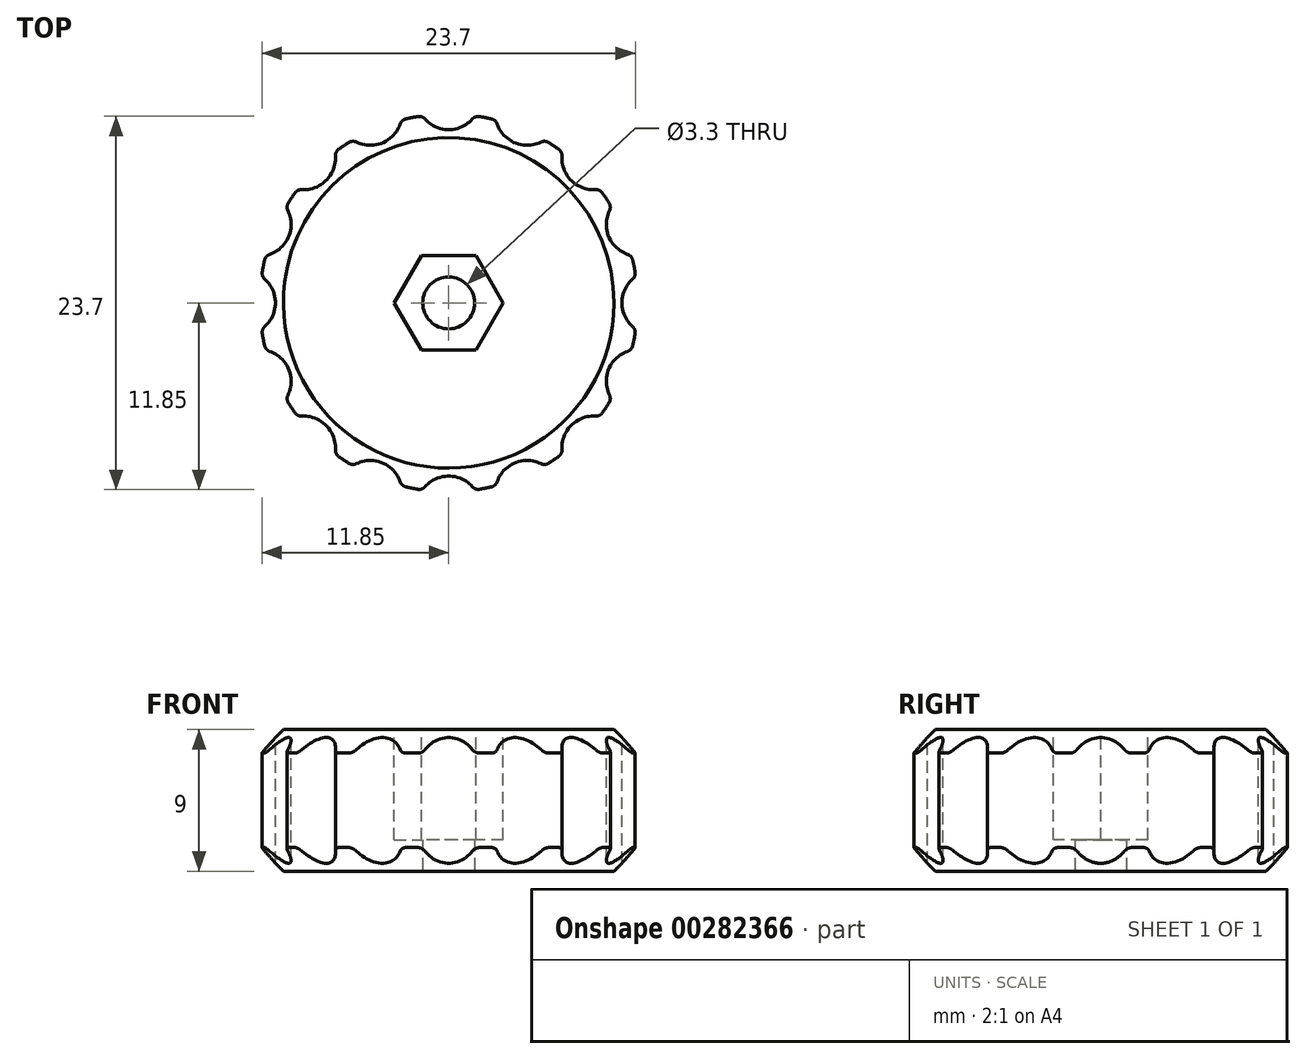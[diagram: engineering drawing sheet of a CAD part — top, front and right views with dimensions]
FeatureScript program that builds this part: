
annotation { "Feature Type Name" : "Feature", "Feature Type Description" : "" }
export const myFeature = defineFeature(function(context is Context, id is Id, definition is map)
    precondition{}
    {
        {
            var Q0;
            Q0=qCreatedBy(makeId("Top.planeOp"),FACE);
            var sketch = newSketch(context, id + "F0", { "sketchPlane" : qUnion([Q0])});
            skCircle(sketch, "E0", {"center": v(0, 0) * mm, "radius": 12 * mm});
            skCircle(sketch, "E1", {"center": v(0, 0) * mm, "radius": 1.65 * mm});
            skSolve(sketch);
        }
        {
            var Q0;
            Q0 = qSketchRegion(id + "F0", true);
            extrude(context, id + "F1", {"entities" : qUnion([Q0]), "depth" : 9 * mm});
        }
        {
            var Q0;
            Q0=makeQuery(id+"F1.opExtrude","CAP_EDGE",EDGE,{"disambiguationData":[OSD([sQuery(id+"F0.wireOp",EDGE,"E0")])],"isStart":false});
            var Q1;
            Q1=makeQuery(id+"F1.opExtrude","CAP_EDGE",EDGE,{"disambiguationData":[OSD([sQuery(id+"F0.wireOp",EDGE,"E0")])],"isStart":true});
            chamfer(context, id + "F2", {"entities" : qUnion([Q0, Q1]), "width" : 1.5 * mm, "tangentPropagation" : true});
        }
        {
            var Q0;
            Q0=makeQuery(id+"F1.opExtrude","CAP_FACE",FACE,{"disambiguationData":[OSD([sQuery(id+"F0.wireOp",EDGE,"E0"),sQuery(id+"F0.wireOp",EDGE,"E1")])],"isStart":false});
            var sketch = newSketch(context, id + "F3", { "sketchPlane" : qUnion([Q0])});
            skCircle(sketch, "E2.cCircle", {"center": v(0, 0) * mm, "radius": 3 * mm, "construction": true});
            skLineSegment(sketch, "E2.0", {"start": v(1.73, -3) * mm, "end": v(-1.73, -3) * mm});
            skLineSegment(sketch, "E2.1", {"start": v(-1.73, -3) * mm, "end": v(-3.46, 0) * mm});
            skLineSegment(sketch, "E2.2", {"start": v(-3.46, 0) * mm, "end": v(-1.73, 3) * mm});
            skLineSegment(sketch, "E2.3", {"start": v(-1.73, 3) * mm, "end": v(1.73, 3) * mm});
            skLineSegment(sketch, "E2.4", {"start": v(1.73, 3) * mm, "end": v(3.46, 0) * mm});
            skLineSegment(sketch, "E2.5", {"start": v(3.46, 0) * mm, "end": v(1.73, -3) * mm});
            skPoint(sketch, "E2.0.midPoint", {"position": v(0, -3) * mm});
            skSolve(sketch);
        }
        {
            var Q0;
            Q0 = qSketchRegion(id + "F3", true);
            extrude(context, id + "F4", {"entities" : qUnion([Q0]), "operationType" : NewBodyOperationType.REMOVE, "oppositeDirection" : true, "depth" : 7 * mm});
        }
        {
            var Q0;
            Q0=makeQuery(id+"F1.opExtrude","CAP_FACE",FACE,{"disambiguationData":[OSD([sQuery(id+"F0.wireOp",EDGE,"E0"),sQuery(id+"F0.wireOp",EDGE,"E1")])],"isStart":false});
            var sketch = newSketch(context, id + "F5", { "sketchPlane" : qUnion([Q0])});
            skLineSegment(sketch, "E3", {"start": v(0, 0) * mm, "end": v(13, 0) * mm, "construction": true});
            skCircle(sketch, "E4", {"center": v(13, 0) * mm, "radius": 2 * mm});
            skCircle(sketch, "E5.1.0", {"center": v(12.01, 4.97) * mm, "radius": 2 * mm});
            skCircle(sketch, "E5.2.0", {"center": v(9.2, 9.2) * mm, "radius": 2 * mm});
            skCircle(sketch, "E5.3.0", {"center": v(4.97, 12.01) * mm, "radius": 2 * mm});
            skCircle(sketch, "E5.4.0", {"center": v(0, 13) * mm, "radius": 2 * mm});
            skCircle(sketch, "E5.5.0", {"center": v(-4.97, 12.01) * mm, "radius": 2 * mm});
            skCircle(sketch, "E5.6.0", {"center": v(-9.2, 9.2) * mm, "radius": 2 * mm});
            skCircle(sketch, "E5.7.0", {"center": v(-12.01, 4.97) * mm, "radius": 2 * mm});
            skCircle(sketch, "E5.8.0", {"center": v(-13, 0) * mm, "radius": 2 * mm});
            skCircle(sketch, "E5.9.0", {"center": v(-12.01, -4.97) * mm, "radius": 2 * mm});
            skCircle(sketch, "E5.10.0", {"center": v(-9.2, -9.2) * mm, "radius": 2 * mm});
            skCircle(sketch, "E5.11.0", {"center": v(-4.97, -12.01) * mm, "radius": 2 * mm});
            skCircle(sketch, "E5.12.0", {"center": v(0, -13) * mm, "radius": 2 * mm});
            skCircle(sketch, "E5.13.0", {"center": v(4.97, -12.01) * mm, "radius": 2 * mm});
            skCircle(sketch, "E5.14.0", {"center": v(9.2, -9.2) * mm, "radius": 2 * mm});
            skCircle(sketch, "E5.15.0", {"center": v(12.01, -4.97) * mm, "radius": 2 * mm});
            skPoint(sketch, "E5.center", {"position": v(0, 0) * mm});
            skSolve(sketch);
        }
        {
            var Q0;
            Q0 = qSketchRegion(id + "F5", true);
            extrude(context, id + "F6", {"entities" : qUnion([Q0]), "operationType" : NewBodyOperationType.REMOVE, "endBound" : BoundingType.THROUGH_ALL, "oppositeDirection" : true, "depth" : 25 * mm});
        }
        {
            var Q0;
            Q0=makeQuery(id+"F6.boolean.opBoolean","INTERSECT",EDGE,{"disambiguationData":[OD(0.0)],"derivedFrom":[makeQuery(id+"F1.opExtrude","SWEPT_FACE",FACE,{"disambiguationData":[OSD([sQuery(id+"F0.wireOp",EDGE,"E0")])]}),makeQuery(id+"F6.opExtrude","SWEPT_FACE",FACE,{"disambiguationData":[OSD([sQuery(id+"F5.wireOp",EDGE,"E5.4.0")])]})]});
            var Q1;
            Q1=makeQuery(id+"F6.boolean.opBoolean","INTERSECT",EDGE,{"disambiguationData":[OD(1.0)],"derivedFrom":[makeQuery(id+"F1.opExtrude","SWEPT_FACE",FACE,{"disambiguationData":[OSD([sQuery(id+"F0.wireOp",EDGE,"E0")])]}),makeQuery(id+"F6.opExtrude","SWEPT_FACE",FACE,{"disambiguationData":[OSD([sQuery(id+"F5.wireOp",EDGE,"E5.3.0")])]})]});
            var Q2;
            Q2=makeQuery(id+"F6.boolean.opBoolean","INTERSECT",EDGE,{"disambiguationData":[OD(0.0)],"derivedFrom":[makeQuery(id+"F1.opExtrude","SWEPT_FACE",FACE,{"disambiguationData":[OSD([sQuery(id+"F0.wireOp",EDGE,"E0")])]}),makeQuery(id+"F6.opExtrude","SWEPT_FACE",FACE,{"disambiguationData":[OSD([sQuery(id+"F5.wireOp",EDGE,"E5.3.0")])]})]});
            var Q3;
            Q3=makeQuery(id+"F6.boolean.opBoolean","INTERSECT",EDGE,{"disambiguationData":[OD(1.0)],"derivedFrom":[makeQuery(id+"F1.opExtrude","SWEPT_FACE",FACE,{"disambiguationData":[OSD([sQuery(id+"F0.wireOp",EDGE,"E0")])]}),makeQuery(id+"F6.opExtrude","SWEPT_FACE",FACE,{"disambiguationData":[OSD([sQuery(id+"F5.wireOp",EDGE,"E5.2.0")])]})]});
            var Q4;
            Q4=makeQuery(id+"F6.boolean.opBoolean","INTERSECT",EDGE,{"disambiguationData":[OD(0.0)],"derivedFrom":[makeQuery(id+"F1.opExtrude","SWEPT_FACE",FACE,{"disambiguationData":[OSD([sQuery(id+"F0.wireOp",EDGE,"E0")])]}),makeQuery(id+"F6.opExtrude","SWEPT_FACE",FACE,{"disambiguationData":[OSD([sQuery(id+"F5.wireOp",EDGE,"E5.2.0")])]})]});
            var Q5;
            Q5=makeQuery(id+"F6.boolean.opBoolean","INTERSECT",EDGE,{"disambiguationData":[OD(1.0)],"derivedFrom":[makeQuery(id+"F1.opExtrude","SWEPT_FACE",FACE,{"disambiguationData":[OSD([sQuery(id+"F0.wireOp",EDGE,"E0")])]}),makeQuery(id+"F6.opExtrude","SWEPT_FACE",FACE,{"disambiguationData":[OSD([sQuery(id+"F5.wireOp",EDGE,"E5.1.0")])]})]});
            var Q6;
            Q6=makeQuery(id+"F6.boolean.opBoolean","INTERSECT",EDGE,{"disambiguationData":[OD(0.0)],"derivedFrom":[makeQuery(id+"F1.opExtrude","SWEPT_FACE",FACE,{"disambiguationData":[OSD([sQuery(id+"F0.wireOp",EDGE,"E0")])]}),makeQuery(id+"F6.opExtrude","SWEPT_FACE",FACE,{"disambiguationData":[OSD([sQuery(id+"F5.wireOp",EDGE,"E5.1.0")])]})]});
            var Q7;
            Q7=makeQuery(id+"F6.boolean.opBoolean","INTERSECT",EDGE,{"disambiguationData":[OD(0.0)],"derivedFrom":[makeQuery(id+"F1.opExtrude","SWEPT_FACE",FACE,{"disambiguationData":[OSD([sQuery(id+"F0.wireOp",EDGE,"E0")])]}),makeQuery(id+"F6.opExtrude","SWEPT_FACE",FACE,{"disambiguationData":[OSD([sQuery(id+"F5.wireOp",EDGE,"E4")])]})]});
            var Q8;
            Q8=makeQuery(id+"F6.boolean.opBoolean","INTERSECT",EDGE,{"disambiguationData":[OD(1.0)],"derivedFrom":[makeQuery(id+"F1.opExtrude","SWEPT_FACE",FACE,{"disambiguationData":[OSD([sQuery(id+"F0.wireOp",EDGE,"E0")])]}),makeQuery(id+"F6.opExtrude","SWEPT_FACE",FACE,{"disambiguationData":[OSD([sQuery(id+"F5.wireOp",EDGE,"E4")])]})]});
            var Q9;
            Q9=makeQuery(id+"F6.boolean.opBoolean","INTERSECT",EDGE,{"disambiguationData":[OD(0.0)],"derivedFrom":[makeQuery(id+"F1.opExtrude","SWEPT_FACE",FACE,{"disambiguationData":[OSD([sQuery(id+"F0.wireOp",EDGE,"E0")])]}),makeQuery(id+"F6.opExtrude","SWEPT_FACE",FACE,{"disambiguationData":[OSD([sQuery(id+"F5.wireOp",EDGE,"E5.15.0")])]})]});
            var Q10;
            Q10=makeQuery(id+"F6.boolean.opBoolean","INTERSECT",EDGE,{"disambiguationData":[OD(1.0)],"derivedFrom":[makeQuery(id+"F1.opExtrude","SWEPT_FACE",FACE,{"disambiguationData":[OSD([sQuery(id+"F0.wireOp",EDGE,"E0")])]}),makeQuery(id+"F6.opExtrude","SWEPT_FACE",FACE,{"disambiguationData":[OSD([sQuery(id+"F5.wireOp",EDGE,"E5.15.0")])]})]});
            var Q11;
            Q11=makeQuery(id+"F6.boolean.opBoolean","INTERSECT",EDGE,{"disambiguationData":[OD(1.0)],"derivedFrom":[makeQuery(id+"F1.opExtrude","SWEPT_FACE",FACE,{"disambiguationData":[OSD([sQuery(id+"F0.wireOp",EDGE,"E0")])]}),makeQuery(id+"F6.opExtrude","SWEPT_FACE",FACE,{"disambiguationData":[OSD([sQuery(id+"F5.wireOp",EDGE,"E5.14.0")])]})]});
            var Q12;
            Q12=makeQuery(id+"F6.boolean.opBoolean","INTERSECT",EDGE,{"disambiguationData":[OD(0.0)],"derivedFrom":[makeQuery(id+"F1.opExtrude","SWEPT_FACE",FACE,{"disambiguationData":[OSD([sQuery(id+"F0.wireOp",EDGE,"E0")])]}),makeQuery(id+"F6.opExtrude","SWEPT_FACE",FACE,{"disambiguationData":[OSD([sQuery(id+"F5.wireOp",EDGE,"E5.14.0")])]})]});
            var Q13;
            Q13=makeQuery(id+"F6.boolean.opBoolean","INTERSECT",EDGE,{"disambiguationData":[OD(1.0)],"derivedFrom":[makeQuery(id+"F1.opExtrude","SWEPT_FACE",FACE,{"disambiguationData":[OSD([sQuery(id+"F0.wireOp",EDGE,"E0")])]}),makeQuery(id+"F6.opExtrude","SWEPT_FACE",FACE,{"disambiguationData":[OSD([sQuery(id+"F5.wireOp",EDGE,"E5.13.0")])]})]});
            var Q14;
            Q14=makeQuery(id+"F6.boolean.opBoolean","INTERSECT",EDGE,{"disambiguationData":[OD(0.0)],"derivedFrom":[makeQuery(id+"F1.opExtrude","SWEPT_FACE",FACE,{"disambiguationData":[OSD([sQuery(id+"F0.wireOp",EDGE,"E0")])]}),makeQuery(id+"F6.opExtrude","SWEPT_FACE",FACE,{"disambiguationData":[OSD([sQuery(id+"F5.wireOp",EDGE,"E5.13.0")])]})]});
            var Q15;
            Q15=makeQuery(id+"F6.boolean.opBoolean","INTERSECT",EDGE,{"disambiguationData":[OD(1.0)],"derivedFrom":[makeQuery(id+"F1.opExtrude","SWEPT_FACE",FACE,{"disambiguationData":[OSD([sQuery(id+"F0.wireOp",EDGE,"E0")])]}),makeQuery(id+"F6.opExtrude","SWEPT_FACE",FACE,{"disambiguationData":[OSD([sQuery(id+"F5.wireOp",EDGE,"E5.12.0")])]})]});
            var Q16;
            Q16=makeQuery(id+"F6.boolean.opBoolean","INTERSECT",EDGE,{"disambiguationData":[OD(0.0)],"derivedFrom":[makeQuery(id+"F1.opExtrude","SWEPT_FACE",FACE,{"disambiguationData":[OSD([sQuery(id+"F0.wireOp",EDGE,"E0")])]}),makeQuery(id+"F6.opExtrude","SWEPT_FACE",FACE,{"disambiguationData":[OSD([sQuery(id+"F5.wireOp",EDGE,"E5.12.0")])]})]});
            var Q17;
            Q17=makeQuery(id+"F6.boolean.opBoolean","INTERSECT",EDGE,{"disambiguationData":[OD(1.0)],"derivedFrom":[makeQuery(id+"F1.opExtrude","SWEPT_FACE",FACE,{"disambiguationData":[OSD([sQuery(id+"F0.wireOp",EDGE,"E0")])]}),makeQuery(id+"F6.opExtrude","SWEPT_FACE",FACE,{"disambiguationData":[OSD([sQuery(id+"F5.wireOp",EDGE,"E5.11.0")])]})]});
            var Q18;
            Q18=makeQuery(id+"F6.boolean.opBoolean","INTERSECT",EDGE,{"disambiguationData":[OD(0.0)],"derivedFrom":[makeQuery(id+"F1.opExtrude","SWEPT_FACE",FACE,{"disambiguationData":[OSD([sQuery(id+"F0.wireOp",EDGE,"E0")])]}),makeQuery(id+"F6.opExtrude","SWEPT_FACE",FACE,{"disambiguationData":[OSD([sQuery(id+"F5.wireOp",EDGE,"E5.11.0")])]})]});
            var Q19;
            Q19=makeQuery(id+"F6.boolean.opBoolean","INTERSECT",EDGE,{"disambiguationData":[OD(1.0)],"derivedFrom":[makeQuery(id+"F1.opExtrude","SWEPT_FACE",FACE,{"disambiguationData":[OSD([sQuery(id+"F0.wireOp",EDGE,"E0")])]}),makeQuery(id+"F6.opExtrude","SWEPT_FACE",FACE,{"disambiguationData":[OSD([sQuery(id+"F5.wireOp",EDGE,"E5.10.0")])]})]});
            var Q20;
            Q20=makeQuery(id+"F6.boolean.opBoolean","INTERSECT",EDGE,{"disambiguationData":[OD(0.0)],"derivedFrom":[makeQuery(id+"F1.opExtrude","SWEPT_FACE",FACE,{"disambiguationData":[OSD([sQuery(id+"F0.wireOp",EDGE,"E0")])]}),makeQuery(id+"F6.opExtrude","SWEPT_FACE",FACE,{"disambiguationData":[OSD([sQuery(id+"F5.wireOp",EDGE,"E5.10.0")])]})]});
            var Q21;
            Q21=makeQuery(id+"F6.boolean.opBoolean","INTERSECT",EDGE,{"disambiguationData":[OD(1.0)],"derivedFrom":[makeQuery(id+"F1.opExtrude","SWEPT_FACE",FACE,{"disambiguationData":[OSD([sQuery(id+"F0.wireOp",EDGE,"E0")])]}),makeQuery(id+"F6.opExtrude","SWEPT_FACE",FACE,{"disambiguationData":[OSD([sQuery(id+"F5.wireOp",EDGE,"E5.9.0")])]})]});
            var Q22;
            Q22=makeQuery(id+"F6.boolean.opBoolean","INTERSECT",EDGE,{"disambiguationData":[OD(0.0)],"derivedFrom":[makeQuery(id+"F1.opExtrude","SWEPT_FACE",FACE,{"disambiguationData":[OSD([sQuery(id+"F0.wireOp",EDGE,"E0")])]}),makeQuery(id+"F6.opExtrude","SWEPT_FACE",FACE,{"disambiguationData":[OSD([sQuery(id+"F5.wireOp",EDGE,"E5.9.0")])]})]});
            var Q23;
            Q23=makeQuery(id+"F6.boolean.opBoolean","INTERSECT",EDGE,{"disambiguationData":[OD(1.0)],"derivedFrom":[makeQuery(id+"F1.opExtrude","SWEPT_FACE",FACE,{"disambiguationData":[OSD([sQuery(id+"F0.wireOp",EDGE,"E0")])]}),makeQuery(id+"F6.opExtrude","SWEPT_FACE",FACE,{"disambiguationData":[OSD([sQuery(id+"F5.wireOp",EDGE,"E5.8.0")])]})]});
            var Q24;
            Q24=makeQuery(id+"F6.boolean.opBoolean","INTERSECT",EDGE,{"disambiguationData":[OD(0.0)],"derivedFrom":[makeQuery(id+"F1.opExtrude","SWEPT_FACE",FACE,{"disambiguationData":[OSD([sQuery(id+"F0.wireOp",EDGE,"E0")])]}),makeQuery(id+"F6.opExtrude","SWEPT_FACE",FACE,{"disambiguationData":[OSD([sQuery(id+"F5.wireOp",EDGE,"E5.8.0")])]})]});
            var Q25;
            Q25=makeQuery(id+"F6.boolean.opBoolean","INTERSECT",EDGE,{"disambiguationData":[OD(1.0)],"derivedFrom":[makeQuery(id+"F1.opExtrude","SWEPT_FACE",FACE,{"disambiguationData":[OSD([sQuery(id+"F0.wireOp",EDGE,"E0")])]}),makeQuery(id+"F6.opExtrude","SWEPT_FACE",FACE,{"disambiguationData":[OSD([sQuery(id+"F5.wireOp",EDGE,"E5.7.0")])]})]});
            var Q26;
            Q26=makeQuery(id+"F6.boolean.opBoolean","INTERSECT",EDGE,{"disambiguationData":[OD(0.0)],"derivedFrom":[makeQuery(id+"F1.opExtrude","SWEPT_FACE",FACE,{"disambiguationData":[OSD([sQuery(id+"F0.wireOp",EDGE,"E0")])]}),makeQuery(id+"F6.opExtrude","SWEPT_FACE",FACE,{"disambiguationData":[OSD([sQuery(id+"F5.wireOp",EDGE,"E5.7.0")])]})]});
            var Q27;
            Q27=makeQuery(id+"F6.boolean.opBoolean","INTERSECT",EDGE,{"disambiguationData":[OD(1.0)],"derivedFrom":[makeQuery(id+"F1.opExtrude","SWEPT_FACE",FACE,{"disambiguationData":[OSD([sQuery(id+"F0.wireOp",EDGE,"E0")])]}),makeQuery(id+"F6.opExtrude","SWEPT_FACE",FACE,{"disambiguationData":[OSD([sQuery(id+"F5.wireOp",EDGE,"E5.6.0")])]})]});
            var Q28;
            Q28=makeQuery(id+"F6.boolean.opBoolean","INTERSECT",EDGE,{"disambiguationData":[OD(1.0)],"derivedFrom":[makeQuery(id+"F1.opExtrude","SWEPT_FACE",FACE,{"disambiguationData":[OSD([sQuery(id+"F0.wireOp",EDGE,"E0")])]}),makeQuery(id+"F6.opExtrude","SWEPT_FACE",FACE,{"disambiguationData":[OSD([sQuery(id+"F5.wireOp",EDGE,"E5.5.0")])]})]});
            var Q29;
            Q29=makeQuery(id+"F6.boolean.opBoolean","INTERSECT",EDGE,{"disambiguationData":[OD(0.0)],"derivedFrom":[makeQuery(id+"F1.opExtrude","SWEPT_FACE",FACE,{"disambiguationData":[OSD([sQuery(id+"F0.wireOp",EDGE,"E0")])]}),makeQuery(id+"F6.opExtrude","SWEPT_FACE",FACE,{"disambiguationData":[OSD([sQuery(id+"F5.wireOp",EDGE,"E5.6.0")])]})]});
            var Q30;
            Q30=makeQuery(id+"F6.boolean.opBoolean","INTERSECT",EDGE,{"disambiguationData":[OD(0.0)],"derivedFrom":[makeQuery(id+"F1.opExtrude","SWEPT_FACE",FACE,{"disambiguationData":[OSD([sQuery(id+"F0.wireOp",EDGE,"E0")])]}),makeQuery(id+"F6.opExtrude","SWEPT_FACE",FACE,{"disambiguationData":[OSD([sQuery(id+"F5.wireOp",EDGE,"E5.5.0")])]})]});
            var Q31;
            Q31=makeQuery(id+"F6.boolean.opBoolean","INTERSECT",EDGE,{"disambiguationData":[OD(1.0)],"derivedFrom":[makeQuery(id+"F1.opExtrude","SWEPT_FACE",FACE,{"disambiguationData":[OSD([sQuery(id+"F0.wireOp",EDGE,"E0")])]}),makeQuery(id+"F6.opExtrude","SWEPT_FACE",FACE,{"disambiguationData":[OSD([sQuery(id+"F5.wireOp",EDGE,"E5.4.0")])]})]});
            fillet(context, id + "F7", {"entities" : qUnion([Q0, Q1, Q2, Q3, Q4, Q5, Q6, Q7, Q8, Q9, Q10, Q11, Q12, Q13, Q14, Q15, Q16, Q17, Q18, Q19, Q20, Q21, Q22, Q23, Q24, Q25, Q26, Q27, Q28, Q29, Q30, Q31]), "radius" : 0.5 * mm, "allowEdgeOverflow" : false});
        }
    });
